# Revit family: ETA-16-0262.GK.012.20 Dauer (standard) L12 - GG-Schutzkappe
name_source: partatom
category: Allgemeines Modell
units: mm (PartAtom-declared; Revit-internal decimal feet)

## family parameters
Arbeitsebenenbasiert = Nein
Beim Laden mit Abzugskörper schneiden = Nein
Bemaßung runder Anschluss = Durchmesser verwenden
Gemeinsam genutzt = Nein
Immer vertikal = Ja
Kann Basisbauteil für Bewehrung sein = Nein
Raumberechnungspunkt = Nein
Teiletyp = Normal

## types (1)
- Norm
    11 Title German = Dauer (standard) L12 - GG-Schutzkappe
    14 Zeichnungsnummer = ETA-16-0262.GK.012.20
    Bauteilnummer = ETA-16-0262.GK.012.20 Dauer (standard) L12 - GG-Schutzkappe
    Beschreibung = Dauerankerkopf (standard) L12 - GG Schutzkappe
    Erstellungsdatum = 22.05.2024 00:00:00
    Hersteller = BBV-Systems
    Modell = ETA-16-0262.GK.012.20.0
    Revisionsnummer = 0
    Vorgabe-Ansicht = 0 mm  [stored 0 ft]

note: [stored X ft] marks values corroborated as IEEE doubles in the binary element streams (Revit-internal decimal feet)
